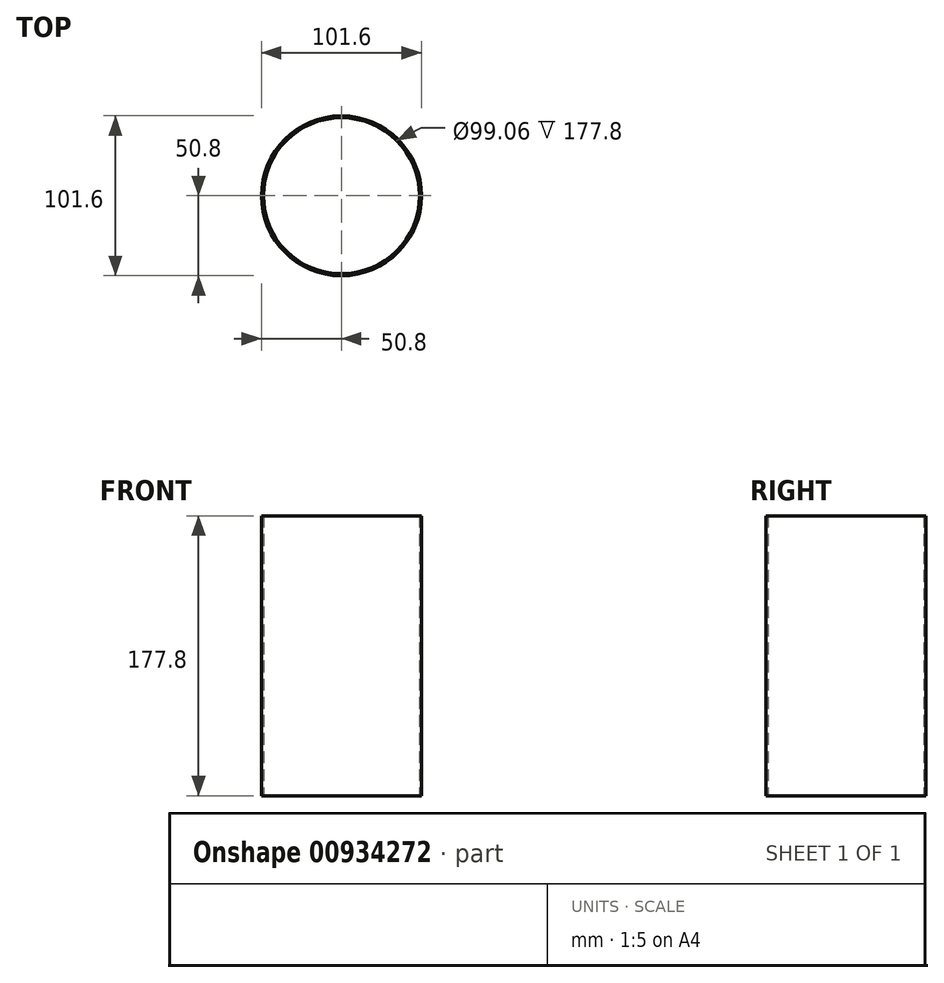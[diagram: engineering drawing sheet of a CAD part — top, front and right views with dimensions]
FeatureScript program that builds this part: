
annotation { "Feature Type Name" : "Feature", "Feature Type Description" : "" }
export const myFeature = defineFeature(function(context is Context, id is Id, definition is map)
    precondition{}
    {
        {
            var Q0;
            Q0=qCreatedBy(makeId("Top.planeOp"),FACE);
            var sketch = newSketch(context, id + "F0", { "sketchPlane" : qUnion([Q0])});
            skCircle(sketch, "E0", {"center": v(0, 0) * mm, "radius": 50.8 * mm});
            skCircle(sketch, "E1", {"center": v(0, 0) * mm, "radius": 49.53 * mm});
            skSolve(sketch);
        }
        {
            var Q0;
            Q0=makeQuery(id+"F0.imprint","IMPRINT",FACE,{"disambiguationData":[TD([[makeQuery(id+"F0.imprint","IMPRINT",EDGE,{"derivedFrom":sQuery(id+"F0.wireOp",EDGE,"E0")}),1.0]])]});
            extrude(context, id + "F1", {"entities" : qUnion([Q0]), "depth" : 177.8 * mm, "offsetDistance" : 25.4 * mm});
        }
    });
